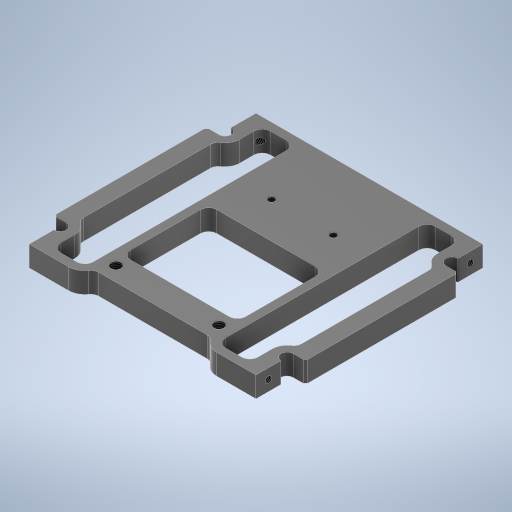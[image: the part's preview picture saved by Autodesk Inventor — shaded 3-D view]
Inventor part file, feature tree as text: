
AUTODESK INVENTOR PART (.ipt)
format: ipt  version: 2024.2 (Build 282272000, 272)  size: 534,528 bytes
history: native  units: mm
features: sketch x2, extrude x1, hole x1, chamfer x1
ambient origin geometry x8: Origin, YZ Plane, XZ Plane, XY Plane, X Axis, Y Axis, Z Axis, Center Point
bodies: Solid1 (feature_tree)
feature tree (5):
  sketch  "Sketch1"  dims[d9=5.0mm d10=0.0mm]
  extrude  "Extrusion1"  Depth=3.0mm
  hole  "Side-M2"  [1 undecoded]
  chamfer  "C0.5"  Distance=55.0mm
  sketch  "Sketch3"  dims[d11=1.567mm d12=4.0mm d13=4.0mm d14=2.0mm d15=90.0deg d16=6.3mm d17=0.0mm d19=3.0mm d20=37.0mm d37=55.0mm d40=6.0mm d41=6.0mm d54=0.5mm d55=2.0mm d56=45.0deg d59=55.0mm d60=1.5mm d61=17.5mm d62=20.0mm d63=15.0mm d102=1.567mm d103=4.0mm d104=4.0mm d105=2.0mm d106=90.0deg d107=6.0mm d108=0.0mm d128=50.0mm d129=32.0mm d130=25.0mm d133=2.459mm d134=6.0mm d135=4.0mm d136=2.0mm d137=90.0deg d138=8.0mm d139=20.594885mm d149=3.5mm d150=2.0mm d152=2.0mm d154=1.0mm d156=16.25mm d158=10.5mm d159=3.5mm d161=2.0mm d162=2.0mm d163=6.0mm]
note: 1 required parameter value undecoded (feature->parameter linkage not recoverable at this tier; creation-order binding heuristic only, values carry confidence <= 0.55)
